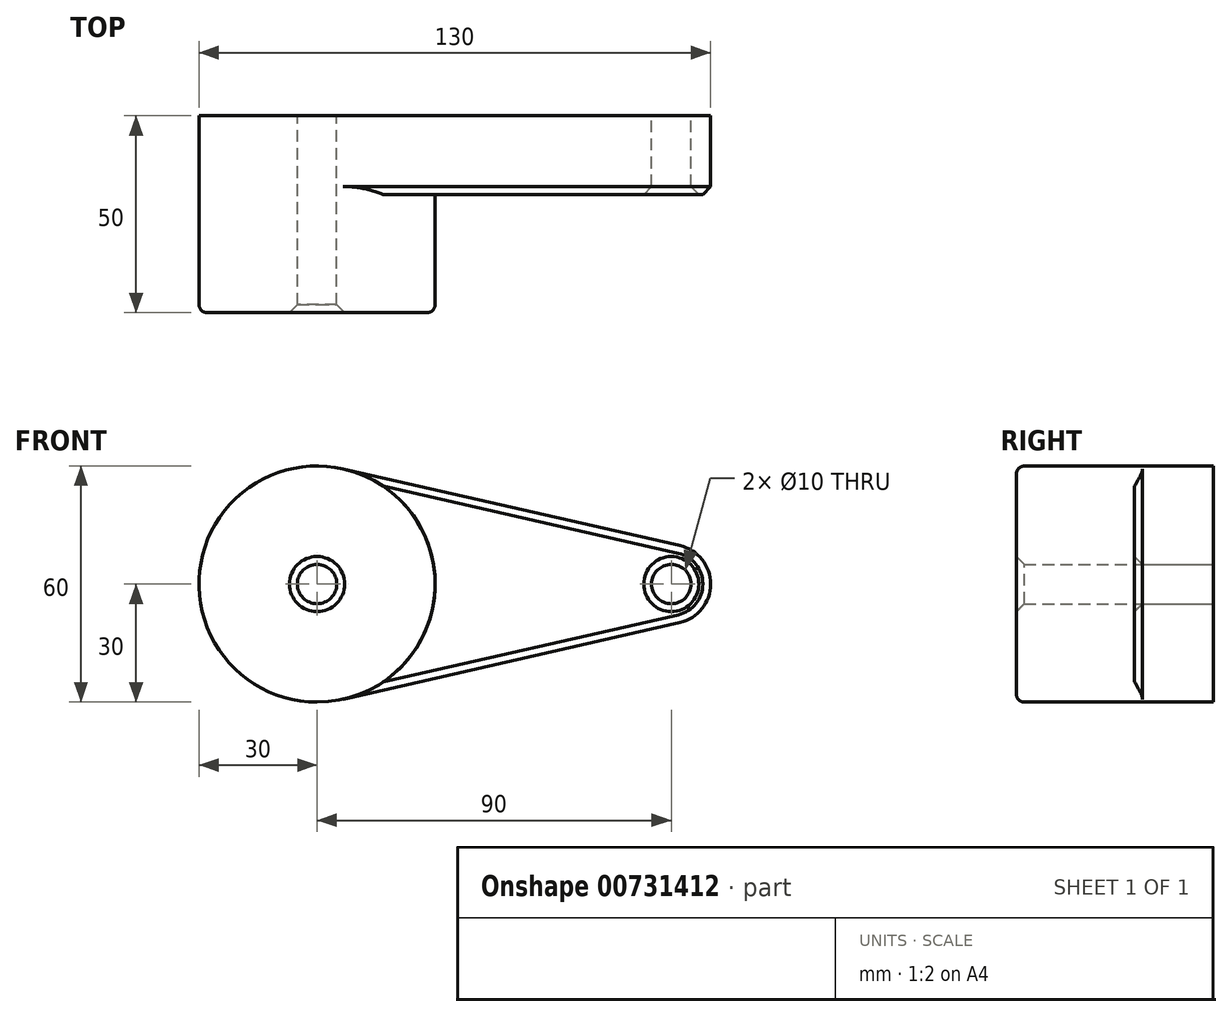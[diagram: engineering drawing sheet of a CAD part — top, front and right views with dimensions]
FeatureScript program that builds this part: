
annotation { "Feature Type Name" : "Feature", "Feature Type Description" : "" }
export const myFeature = defineFeature(function(context is Context, id is Id, definition is map)
    precondition{}
    {
        {
            var Q0;
            Q0=qCreatedBy(makeId("Front.planeOp"),FACE);
            var sketch = newSketch(context, id + "F0", { "sketchPlane" : qUnion([Q0])});
            skCircle(sketch, "E0", {"center": v(0, 0) * mm, "radius": 30 * mm});
            skCircle(sketch, "E1", {"center": v(90, 0) * mm, "radius": 10 * mm});
            skLineSegment(sketch, "E2", {"start": v(0, 0) * mm, "end": v(90, 0) * mm, "construction": true});
            skLineSegment(sketch, "E3", {"start": v(6.67, -29.25) * mm, "end": v(92.22, -9.75) * mm});
            skLineSegment(sketch, "E4", {"start": v(6.67, 29.25) * mm, "end": v(92.22, 9.75) * mm});
            skCircle(sketch, "E5", {"center": v(90, 0) * mm, "radius": 5 * mm});
            skCircle(sketch, "E6", {"center": v(0, 0) * mm, "radius": 5 * mm});
            skSolve(sketch);
        }
        {
            var Q0;
            Q0=makeQuery(id+"F0.imprint","IMPRINT",FACE,{"disambiguationData":[TD([[makeQuery(id+"F0.imprint","IMPRINT",EDGE,{"derivedFrom":sQuery(id+"F0.wireOp",EDGE,"E6")}),-1.0]])]});
            var Q1;
            {var subQ0=sQuery(id+"F0.wireOp",EDGE,"E3");Q1=makeQuery(id+"F0.imprint","IMPRINT",FACE,{"disambiguationData":[TD([[makeQuery(id+"F0.imprint","IMPRINT",EDGE,{"derivedFrom":subQ0}),1.0]])]});}
            var Q2;
            Q2=makeQuery(id+"F0.imprint","IMPRINT",FACE,{"disambiguationData":[TD([[makeQuery(id+"F0.imprint","IMPRINT",EDGE,{"derivedFrom":sQuery(id+"F0.wireOp",EDGE,"E5")}),-1.0]])]});
            extrude(context, id + "F1", {"entities" : qUnion([Q0, Q1, Q2]), "depth" : 20 * mm, "offsetDistance" : 25 * mm});
        }
        {
            var Q0;
            Q0=makeQuery(id+"F0.imprint","IMPRINT",FACE,{"disambiguationData":[TD([[makeQuery(id+"F0.imprint","IMPRINT",EDGE,{"derivedFrom":sQuery(id+"F0.wireOp",EDGE,"E6")}),-1.0]])]});
            extrude(context, id + "F2", {"entities" : qUnion([Q0]), "operationType" : NewBodyOperationType.ADD, "depth" : 50 * mm, "offsetDistance" : 25 * mm});
        }
        {
            var Q0;
            Q0=makeQuery(id+"F2.opExtrude","CAP_EDGE",EDGE,{"disambiguationData":[OSD([sQuery(id+"F0.wireOp",EDGE,"E0")])],"isStart":false});
            fillet(context, id + "F3", {"entities" : qUnion([Q0]), "radius" : 2 * mm, "tangentPropagation" : true, "allowEdgeOverflow" : false});
        }
        {
            var Q0;
            Q0=makeQuery(id+"F2.opExtrude","CAP_EDGE",EDGE,{"disambiguationData":[OSD([sQuery(id+"F0.wireOp",EDGE,"E6")])],"isStart":false});
            var Q1;
            Q1=makeQuery(id+"F1.opExtrude","CAP_EDGE",EDGE,{"disambiguationData":[OSD([sQuery(id+"F0.wireOp",EDGE,"E4")])],"isStart":false});
            var Q2;
            Q2=makeQuery(id+"F1.opExtrude","CAP_EDGE",EDGE,{"disambiguationData":[OSD([sQuery(id+"F0.wireOp",EDGE,"E3")])],"isStart":false});
            var Q3;
            Q3=makeQuery(id+"F1.opExtrude","CAP_EDGE",EDGE,{"disambiguationData":[OSD([sQuery(id+"F0.wireOp",EDGE,"E5")])],"isStart":false});
            chamfer(context, id + "F4", {"entities" : qUnion([Q0, Q1, Q2, Q3]), "width" : 2 * mm, "tangentPropagation" : true});
        }
    });
